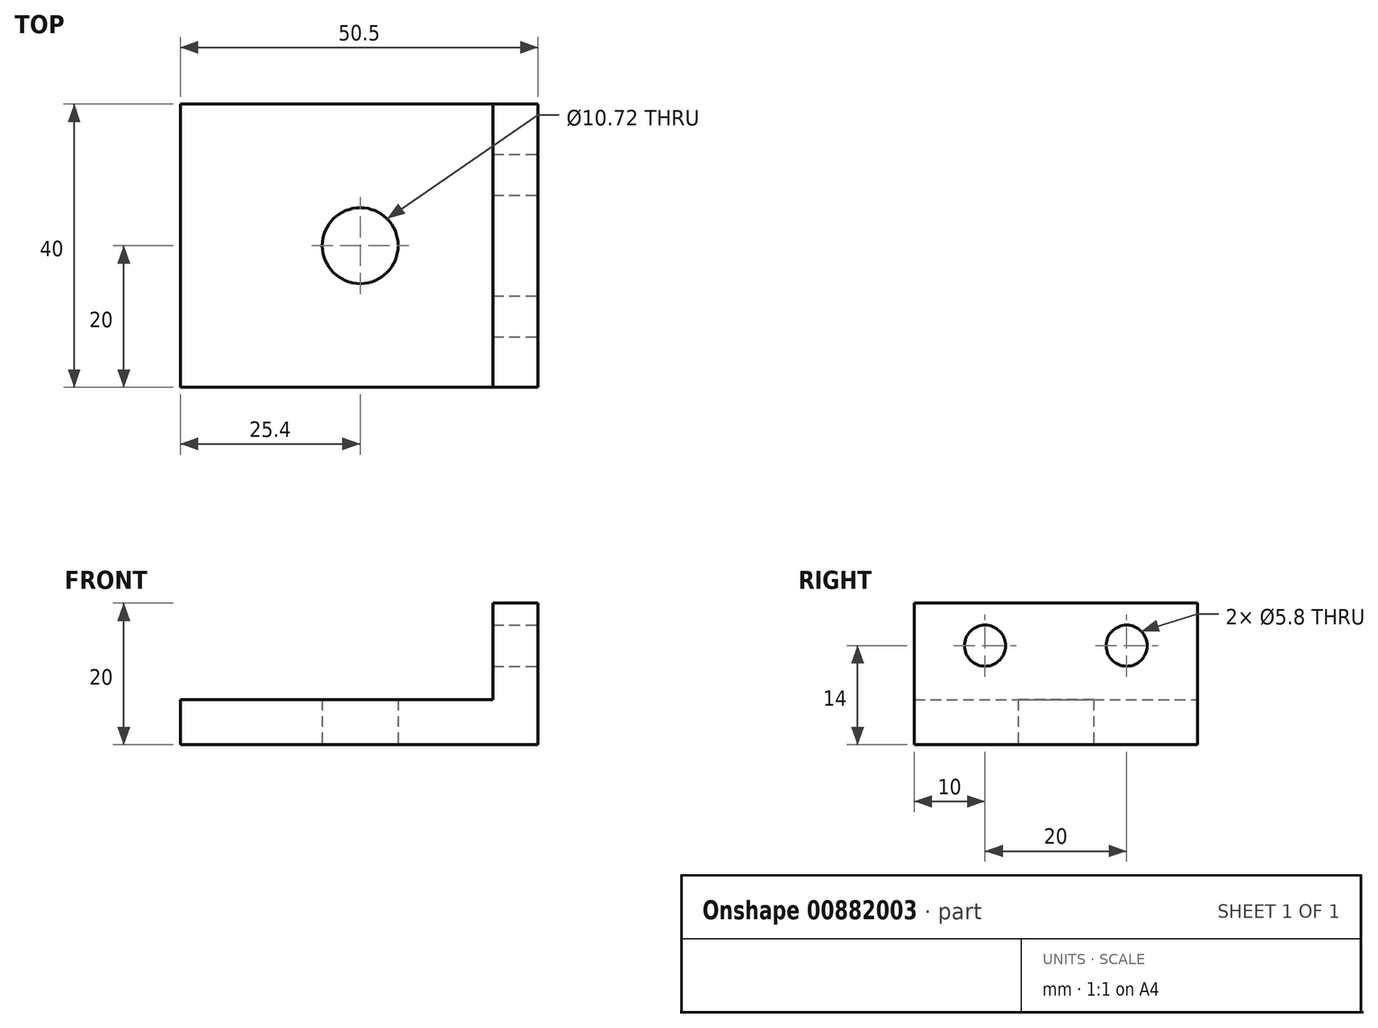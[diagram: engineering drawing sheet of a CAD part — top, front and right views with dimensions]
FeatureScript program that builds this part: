
annotation { "Feature Type Name" : "Feature", "Feature Type Description" : "" }
export const myFeature = defineFeature(function(context is Context, id is Id, definition is map)
    precondition{}
    {
        {
            var Q0;
            Q0=qCreatedBy(makeId("Right.planeOp"),FACE);
            var sketch = newSketch(context, id + "F0", { "sketchPlane" : qUnion([Q0])});
            skLineSegment(sketch, "E0.bottom", {"start": v(0, 0) * mm, "end": v(40, 0) * mm});
            skLineSegment(sketch, "E0.top", {"start": v(0, 20) * mm, "end": v(40, 20) * mm});
            skLineSegment(sketch, "E0.left", {"start": v(0, 0) * mm, "end": v(0, 20) * mm});
            skLineSegment(sketch, "E0.right", {"start": v(40, 0) * mm, "end": v(40, 20) * mm});
            skPoint(sketch, "E1", {"position": v(30, 14) * mm});
            skPoint(sketch, "E2", {"position": v(10, 14) * mm});
            skSolve(sketch);
        }
        {
            var Q0;
            Q0 = qSketchRegion(id + "F0", true);
            var Q1;
            Q1=makeQuery(id+"F0.imprint","IMPRINT",FACE,{"disambiguationData":[TD([[makeQuery(id+"F0.imprint","IMPRINT",EDGE,{"derivedFrom":sQuery(id+"F0.wireOp",EDGE,"E0.bottom")}),1.0]])]});
            extrude(context, id + "F1", {"entities" : qUnion([Q0, Q1]), "depth" : 6.35 * mm, "offsetDistance" : 25 * mm});
        }
        {
            var Q0;
            Q0=makeQuery(id+"F1.opExtrude","CAP_FACE",FACE,{"disambiguationData":[OSD([sQuery(id+"F0.wireOp",EDGE,"E0.bottom"),sQuery(id+"F0.wireOp",EDGE,"E0.top"),sQuery(id+"F0.wireOp",EDGE,"E0.left"),sQuery(id+"F0.wireOp",EDGE,"E0.right")])],"isStart":true});
            var sketch = newSketch(context, id + "F2", { "sketchPlane" : qUnion([Q0])});
            skLineSegment(sketch, "E3", {"start": v(0, 6.35) * mm, "end": v(-40, 6.35) * mm});
            skSolve(sketch);
        }
        {
            var Q0;
            Q0 = qSketchRegion(id + "F2", true);
            var Q1;
            {var subQ0=sQuery(id+"F2.wireOp",EDGE,"E3");Q1=makeQuery(id+"F2.imprint","IMPRINT",FACE,{"disambiguationData":[TD([[makeQuery(id+"F2.imprint","IMPRINT",EDGE,{"derivedFrom":subQ0}),1.0]])]});}
            extrude(context, id + "F3", {"entities" : qUnion([Q0, Q1]), "operationType" : NewBodyOperationType.ADD, "depth" : (50.5 - 6.35) * mm, "offsetDistance" : 25 * mm});
        }
        {
            var Q0;
            Q0=makeQuery(id+"F3.opExtrude","SWEPT_FACE",FACE,{"disambiguationData":[OSD([sQuery(id+"F2.wireOp",EDGE,"E3")])]});
            var sketch = newSketch(context, id + "F4", { "sketchPlane" : qUnion([Q0])});
            skPoint(sketch, "E4", {"position": v(-18.75, 20) * mm});
            skSolve(sketch);
        }
        {
            var Q0;
            Q0=sQuery(id+"F4.wireOp",VERTEX,"E4");
            var Q1;
            Q1=makeQuery(id+"F1.opExtrude","SWEPT_BODY",BODY,{"disambiguationData":[OSD([sQuery(id+"F0.wireOp",EDGE,"E0.bottom"),sQuery(id+"F0.wireOp",EDGE,"E0.top"),sQuery(id+"F0.wireOp",EDGE,"E0.left"),sQuery(id+"F0.wireOp",EDGE,"E0.right")])]});
            hole(context, id + "F5", {"style" : HoleStyle.SIMPLE, "endStyle" : HoleEndStyle.BLIND, "standardTappedOrClearance" : lookupTablePath({ "fit" : "Loose (ASME)", "standard" : "ANSI", "size" : "3/8", "type" : "Clearance" }), "standardBlindInLast" : lookupTablePath({ "fit" : "Loose", "standard" : "ANSI", "size" : "3/8", "type" : "Clearance" }), "holeDiameter" : 10.72 * mm, "majorDiameter" : 5 * mm, "holeDepth" : 12.7 * mm, "isTappedThrough" : true, "tappedDepth" : 9.53 * mm, "tapClearance" : 3, "locations" : qUnion([Q0]), "scope" : qUnion([Q1]), "startStyle" : HoleStartStyle.SKETCH});
        }
        {
            var Q0;
            Q0=sQuery(id+"F0.wireOp",VERTEX,"E1");
            var Q1;
            Q1=sQuery(id+"F0.wireOp",VERTEX,"E2");
            var Q2;
            Q2=makeQuery(id+"F1.opExtrude","SWEPT_BODY",BODY,{"disambiguationData":[OSD([sQuery(id+"F0.wireOp",EDGE,"E0.bottom"),sQuery(id+"F0.wireOp",EDGE,"E0.top"),sQuery(id+"F0.wireOp",EDGE,"E0.left"),sQuery(id+"F0.wireOp",EDGE,"E0.right")])]});
            hole(context, id + "F6", {"style" : HoleStyle.SIMPLE, "endStyle" : HoleEndStyle.BLIND, "oppositeDirection" : true, "standardTappedOrClearance" : lookupTablePath({ "fit" : "Loose", "standard" : "ISO", "size" : "M5", "type" : "Clearance" }), "standardBlindInLast" : lookupTablePath({ "fit" : "Loose", "standard" : "ISO", "size" : "M5", "type" : "Clearance" }), "holeDiameter" : 5.8 * mm, "majorDiameter" : 5 * mm, "holeDepth" : 12.7 * mm, "isTappedThrough" : true, "tappedDepth" : 9.53 * mm, "tapClearance" : 3, "locations" : qUnion([Q0, Q1]), "scope" : qUnion([Q2]), "startStyle" : HoleStartStyle.SKETCH});
        }
    });
